# Revit family: Gira_020830
name_source: partatom
category: Electrical Fixtures
revit_build: Autodesk Revit 2017 (Build: 20160225_1515(x64)
units: mm (PartAtom-declared; Revit-internal decimal feet)

## family parameters
Cut with Voids When Loaded = No
Host = Face
Maintain Annotation Orientation = Yes
Part Type = Normal
Room Calculation Point = No
Round Connector Dimension = Use Diameter
Shared = No

## types (1)
- Cover plate Glass pl. of in.sp. WP surface-mounted yellow
    Available = No
    BIM (1) = https://media.stage.bim.site und Tasten.rfa?public/gira/36a6b08/IP44_Komplettgerät_Schalten und Tasten.rfa
    Category = Control element/cover plate for domestic switching devices
    Colour = Yellow
    Data sheet (1) = https://katalog.gira.de
    Default Elevation = 1219 mm
    Description = Cov.pl.in.sp.pane WP SM YE,Cover plate with inscription space and glass pane suitable for water-protected rocker switches, indicator switches, and buttons,,yellow RAL 1018,Notes :,- Not suitable for 3-pole switches.
    GTIN = 4010337208303
    HAN = 020830
    Halogen free = Yes
    HeinzeBIM = https://bimportal.heinze.de
    Imprint/indication = Without imprint
    Manufacturer = Gira
    Manufacturer URL = https://www.gira.de
    Material = Other
    Material quality = Other
    Model = Single rocker
    Monitoring window/light outlet = No
    Name = Cover plate Glass pl. of in.sp. WP surface-mounted yellow
    RAL-number (akin) = 1018
    Scannable symbol / barrier free = No
    Suitable for degree of protection (IP) = IP20
    Suitable for touch sensor connector for bus system = No
    Surface protection = Other
    Type of fastening = Screw mounting
    URL = http://katalog.gira.de
    Utilization = Switch/push button
    With exchangeable lens/symbol = Yes
    With label area = Yes

## geometry (parser evidence)
native form markers: Sweep x1
no freeform markers — native parametric forms only
